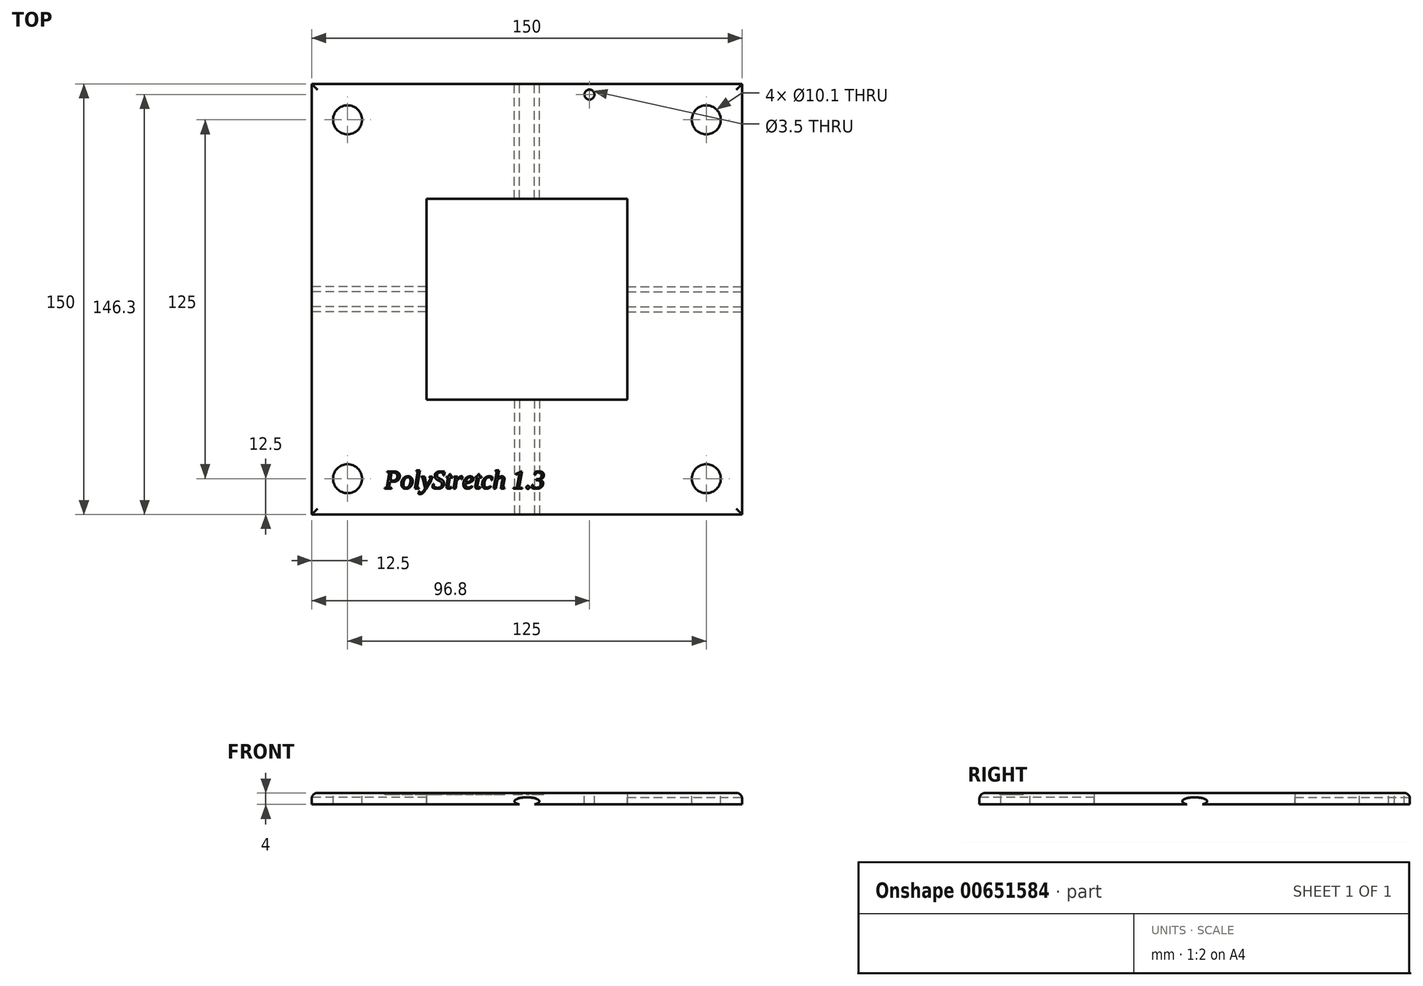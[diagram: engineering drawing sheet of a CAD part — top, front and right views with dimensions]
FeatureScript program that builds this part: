
annotation { "Feature Type Name" : "Feature", "Feature Type Description" : "" }
export const myFeature = defineFeature(function(context is Context, id is Id, definition is map)
    precondition{}
    {
        {
            var Q0;
            Q0=qCreatedBy(makeId("Top.planeOp"),FACE);
            var sketch = newSketch(context, id + "F0", { "sketchPlane" : qUnion([Q0])});
            skLineSegment(sketch, "E0.bottom", {"start": v(75, 75) * mm, "end": v(-75, 75) * mm});
            skLineSegment(sketch, "E0.top", {"start": v(75, -75) * mm, "end": v(-75, -75) * mm});
            skLineSegment(sketch, "E0.left", {"start": v(75, 75) * mm, "end": v(75, -75) * mm});
            skLineSegment(sketch, "E0.right", {"start": v(-75, 75) * mm, "end": v(-75, -75) * mm});
            skPoint(sketch, "E0.middle", {"position": v(0, 0) * mm});
            skLineSegment(sketch, "E1.bottom", {"start": v(35, 35) * mm, "end": v(-35, 35) * mm});
            skLineSegment(sketch, "E1.top", {"start": v(35, -35) * mm, "end": v(-35, -35) * mm});
            skLineSegment(sketch, "E1.left", {"start": v(35, 35) * mm, "end": v(35, -35) * mm});
            skLineSegment(sketch, "E1.right", {"start": v(-35, 35) * mm, "end": v(-35, -35) * mm});
            skSolve(sketch);
        }
        {
            var Q0;
            Q0=makeQuery(id+"F0.imprint","IMPRINT",FACE,{"disambiguationData":[TD([[makeQuery(id+"F0.imprint","IMPRINT",EDGE,{"derivedFrom":sQuery(id+"F0.wireOp",EDGE,"E0.bottom")}),1.0]])]});
            var Q1;
            Q1=makeQuery(id+"F0.imprint","IMPRINT",FACE,{"disambiguationData":[TD([[makeQuery(id+"F0.imprint","IMPRINT",EDGE,{"derivedFrom":sQuery(id+"F0.wireOp",EDGE,"3oa3hqku-FSQT-L0BX-7M5J-21aA9cYNgIiB")}),1.0]])]});
            extrude(context, id + "F1", {"entities" : qUnion([Q0, Q1]), "depth" : 4 * mm});
        }
        {
            var Q0;
            Q0=makeQuery(id+"F1.opExtrude","CAP_FACE",FACE,{"disambiguationData":[OSD([sQuery(id+"F0.wireOp",EDGE,"E0.bottom"),sQuery(id+"F0.wireOp",EDGE,"E0.top"),sQuery(id+"F0.wireOp",EDGE,"E0.left"),sQuery(id+"F0.wireOp",EDGE,"E0.right"),sQuery(id+"F0.wireOp",EDGE,"E1.bottom"),sQuery(id+"F0.wireOp",EDGE,"E1.top"),sQuery(id+"F0.wireOp",EDGE,"E1.left"),sQuery(id+"F0.wireOp",EDGE,"E1.right")])],"isStart":false});
            var sketch = newSketch(context, id + "F2", { "sketchPlane" : qUnion([Q0])});
            skLineSegment(sketch, "E2", {"start": v(-62.5, -75) * mm, "end": v(-62.5, -62.5) * mm, "construction": true});
            skLineSegment(sketch, "E3", {"start": v(-62.5, -62.5) * mm, "end": v(-75, -62.5) * mm, "construction": true});
            skCircle(sketch, "E4", {"center": v(-62.5, -62.5) * mm, "radius": 5.05 * mm});
            skLineSegment(sketch, "E5", {"start": v(-62.5, 75) * mm, "end": v(-62.5, 62.5) * mm, "construction": true});
            skLineSegment(sketch, "E6", {"start": v(-62.5, 62.5) * mm, "end": v(-75, 62.5) * mm, "construction": true});
            skLineSegment(sketch, "E7", {"start": v(62.5, 75) * mm, "end": v(62.5, 62.5) * mm, "construction": true});
            skLineSegment(sketch, "E8", {"start": v(62.5, 62.5) * mm, "end": v(75, 62.5) * mm, "construction": true});
            skLineSegment(sketch, "E9", {"start": v(75, -62.5) * mm, "end": v(62.5, -62.5) * mm, "construction": true});
            skLineSegment(sketch, "E10", {"start": v(62.5, -62.5) * mm, "end": v(62.5, -75) * mm, "construction": true});
            skCircle(sketch, "E11", {"center": v(-62.5, 62.5) * mm, "radius": 5.05 * mm});
            skCircle(sketch, "E12", {"center": v(62.5, 62.5) * mm, "radius": 5.05 * mm});
            skCircle(sketch, "E13", {"center": v(62.5, -62.5) * mm, "radius": 5.05 * mm});
            skSolve(sketch);
        }
        {
            var Q0;
            Q0=makeQuery(id+"F2.imprint","IMPRINT",FACE,{"disambiguationData":[TD([[makeQuery(id+"F2.imprint","IMPRINT",EDGE,{"derivedFrom":sQuery(id+"F2.wireOp",EDGE,"E12")}),1.0]])]});
            var Q1;
            Q1=makeQuery(id+"F2.imprint","IMPRINT",FACE,{"disambiguationData":[TD([[makeQuery(id+"F2.imprint","IMPRINT",EDGE,{"derivedFrom":sQuery(id+"F2.wireOp",EDGE,"E11")}),1.0]])]});
            var Q2;
            Q2=makeQuery(id+"F2.imprint","IMPRINT",FACE,{"disambiguationData":[TD([[makeQuery(id+"F2.imprint","IMPRINT",EDGE,{"derivedFrom":sQuery(id+"F2.wireOp",EDGE,"E4")}),1.0]])]});
            var Q3;
            Q3=makeQuery(id+"F2.imprint","IMPRINT",FACE,{"disambiguationData":[TD([[makeQuery(id+"F2.imprint","IMPRINT",EDGE,{"derivedFrom":sQuery(id+"F2.wireOp",EDGE,"E13")}),1.0]])]});
            extrude(context, id + "F3", {"entities" : qUnion([Q0, Q1, Q2, Q3]), "operationType" : NewBodyOperationType.REMOVE, "oppositeDirection" : true, "depth" : 4 * mm});
        }
        {
            var Q0;
            Q0=makeQuery(id+"F1.opExtrude","CAP_FACE",FACE,{"disambiguationData":[OSD([sQuery(id+"F0.wireOp",EDGE,"E0.bottom"),sQuery(id+"F0.wireOp",EDGE,"E0.top"),sQuery(id+"F0.wireOp",EDGE,"E0.left"),sQuery(id+"F0.wireOp",EDGE,"E0.right"),sQuery(id+"F0.wireOp",EDGE,"E1.bottom"),sQuery(id+"F0.wireOp",EDGE,"E1.top"),sQuery(id+"F0.wireOp",EDGE,"E1.left"),sQuery(id+"F0.wireOp",EDGE,"E1.right")])],"isStart":false});
            var sketch = newSketch(context, id + "F4", { "sketchPlane" : qUnion([Q0])});
            skText(sketch, "E14", { "text": "PolyStretch 1.3", "fontName": "Tinos-Italic.ttf"});
            const initialGuessF4  = {"E14": [-0.0496, -0.06594, 1, 0, 0.00652]};
            skSetInitialGuess(sketch, initialGuessF4);
            skSolve(sketch);
        }
        {
            var Q0;
            Q0=qSketchRegion(id+"F4",true);
            extrude(context, id + "F5", {"entities" : qUnion([Q0]), "operationType" : NewBodyOperationType.REMOVE, "oppositeDirection" : true, "depth" : 0.5 * mm});
        }
        {
            var Q0;
            Q0=makeQuery(id+"F1.opExtrude","SWEPT_FACE",FACE,{"disambiguationData":[OSD([sQuery(id+"F0.wireOp",EDGE,"E0.top")])]});
            var sketch = newSketch(context, id + "F6", { "sketchPlane" : qUnion([Q0])});
            skPoint(sketch, "E15.centerSnap0", {"position": v(0, 0) * mm});
            skLineSegment(sketch, "E16", {"start": v(0, 0) * mm, "end": v(0, 1.1) * mm, "construction": true});
            skEllipse(sketch, "E17", {"center": v(0, 1.1) * mm, "majorRadius": 4.33 * mm, "minorRadius": 1.38 * mm, "majorAxis": v(-1, 0)});
            skSolve(sketch);
        }
        {
            var Q0;
            {var subQ0=sQuery(id+"F6.wireOp",EDGE,"E17");var subQ1=makeQuery(id+"F1.opExtrude","CAP_EDGE",EDGE,{"disambiguationData":[OSD([sQuery(id+"F0.wireOp",EDGE,"E0.top")])],"isStart":true});var subQ2=makeQuery(id+"F6.imprint","INTERSECT",VERTEX,{"disambiguationData":[OD(0.0)],"derivedFrom":[subQ1,subQ0]});Q0=makeQuery(id+"F6.imprint","IMPRINT",FACE,{"disambiguationData":[TD([[makeQuery(id+"F6.imprint","IMPRINT",EDGE,{"disambiguationData":[TD([[subQ2,-1.0]])],"derivedFrom":subQ0}),1.0]])]});}
            extrude(context, id + "F7", {"entities" : qUnion([Q0]), "operationType" : NewBodyOperationType.REMOVE, "oppositeDirection" : true, "depth" : 50 * mm});
        }
        {
            var Q0;
            Q0=makeQuery(id+"F1.opExtrude","SWEPT_FACE",FACE,{"disambiguationData":[OSD([sQuery(id+"F0.wireOp",EDGE,"E0.left")])]});
            var sketch = newSketch(context, id + "F8", { "sketchPlane" : qUnion([Q0])});
            skPoint(sketch, "E18.centerSnap0", {"position": v(0, 0) * mm});
            skLineSegment(sketch, "E19", {"start": v(0, 0) * mm, "end": v(0, 1.1) * mm, "construction": true});
            skEllipse(sketch, "E20", {"center": v(0, 1.1) * mm, "majorRadius": 4.33 * mm, "minorRadius": 1.38 * mm, "majorAxis": v(1, 0)});
            skSolve(sketch);
        }
        {
            var Q0;
            Q0=qSketchRegion(id+"F8",true);
            extrude(context, id + "F9", {"entities" : qUnion([Q0]), "operationType" : NewBodyOperationType.REMOVE, "oppositeDirection" : true, "depth" : 50 * mm});
        }
        {
            var Q0;
            Q0=makeQuery(id+"F1.opExtrude","SWEPT_FACE",FACE,{"disambiguationData":[OSD([sQuery(id+"F0.wireOp",EDGE,"E0.right")])]});
            var sketch = newSketch(context, id + "F10", { "sketchPlane" : qUnion([Q0])});
            skLineSegment(sketch, "E21", {"start": v(0, 0) * mm, "end": v(0, 1.1) * mm, "construction": true});
            skEllipse(sketch, "E22", {"center": v(0, 1.1) * mm, "majorRadius": 4.33 * mm, "minorRadius": 1.38 * mm, "majorAxis": v(-1, 0)});
            skSolve(sketch);
        }
        {
            var Q0;
            {var subQ0=sQuery(id+"F10.wireOp",EDGE,"E22");var subQ1=makeQuery(id+"F1.opExtrude","CAP_EDGE",EDGE,{"disambiguationData":[OSD([sQuery(id+"F0.wireOp",EDGE,"E0.right")])],"isStart":true});var subQ2=makeQuery(id+"F10.imprint","INTERSECT",VERTEX,{"disambiguationData":[OD(0.0)],"derivedFrom":[subQ1,subQ0]});Q0=makeQuery(id+"F10.imprint","IMPRINT",FACE,{"disambiguationData":[TD([[makeQuery(id+"F10.imprint","IMPRINT",EDGE,{"disambiguationData":[TD([[subQ2,1.0]])],"derivedFrom":subQ0}),1.0]])]});}
            extrude(context, id + "F11", {"entities" : qUnion([Q0]), "operationType" : NewBodyOperationType.REMOVE, "oppositeDirection" : true, "depth" : 50 * mm});
        }
        {
            var Q0;
            Q0=makeQuery(id+"F1.opExtrude","SWEPT_FACE",FACE,{"disambiguationData":[OSD([sQuery(id+"F0.wireOp",EDGE,"E0.bottom")])]});
            var sketch = newSketch(context, id + "F12", { "sketchPlane" : qUnion([Q0])});
            skLineSegment(sketch, "E23", {"start": v(0, 0) * mm, "end": v(0, 1.1) * mm, "construction": true});
            skEllipse(sketch, "E24", {"center": v(0, 1.1) * mm, "majorRadius": 4.33 * mm, "minorRadius": 1.38 * mm, "majorAxis": v(-1, 0)});
            skSolve(sketch);
        }
        {
            var Q0;
            {var subQ0=sQuery(id+"F12.wireOp",EDGE,"E24");var subQ1=makeQuery(id+"F1.opExtrude","CAP_EDGE",EDGE,{"disambiguationData":[OSD([sQuery(id+"F0.wireOp",EDGE,"E0.bottom")])],"isStart":true});var subQ2=makeQuery(id+"F12.imprint","INTERSECT",VERTEX,{"disambiguationData":[OD(0.0)],"derivedFrom":[subQ1,subQ0]});Q0=makeQuery(id+"F12.imprint","IMPRINT",FACE,{"disambiguationData":[TD([[makeQuery(id+"F12.imprint","IMPRINT",EDGE,{"disambiguationData":[TD([[subQ2,1.0]])],"derivedFrom":subQ0}),1.0]])]});}
            extrude(context, id + "F13", {"entities" : qUnion([Q0]), "operationType" : NewBodyOperationType.REMOVE, "oppositeDirection" : true, "depth" : 50 * mm});
        }
        {
            var Q0;
            Q0=makeQuery(id+"F1.opExtrude","CAP_EDGE",EDGE,{"disambiguationData":[OSD([sQuery(id+"F0.wireOp",EDGE,"E0.left")])],"isStart":false});
            var Q1;
            Q1=makeQuery(id+"F1.opExtrude","CAP_EDGE",EDGE,{"disambiguationData":[OSD([sQuery(id+"F0.wireOp",EDGE,"E0.bottom")])],"isStart":false});
            var Q2;
            Q2=makeQuery(id+"F1.opExtrude","CAP_EDGE",EDGE,{"disambiguationData":[OSD([sQuery(id+"F0.wireOp",EDGE,"E0.top")])],"isStart":false});
            var Q3;
            Q3=makeQuery(id+"F1.opExtrude","CAP_EDGE",EDGE,{"disambiguationData":[OSD([sQuery(id+"F0.wireOp",EDGE,"E0.right")])],"isStart":false});
            fillet(context, id + "F14", {"entities" : qUnion([Q0, Q1, Q2, Q3]), "radius" : 2 * mm, "tangentPropagation" : true, "allowEdgeOverflow" : false});
        }
        {
            var Q0;
            {var subQ0=sQuery(id+"F0.wireOp",EDGE,"E1.left");var subQ1=sQuery(id+"F0.wireOp",EDGE,"E1.right");var subQ2=sQuery(id+"F0.wireOp",EDGE,"E1.top");var subQ3=sQuery(id+"F0.wireOp",EDGE,"E0.bottom");var subQ4=sQuery(id+"F0.wireOp",EDGE,"E0.top");var subQ5=sQuery(id+"F0.wireOp",EDGE,"E1.bottom");var subQ6=sQuery(id+"F0.wireOp",EDGE,"E0.left");var subQ7=sQuery(id+"F0.wireOp",EDGE,"E0.right");Q0=makeQuery(id+"F5.boolean.opBoolean","SPLIT",FACE,{"disambiguationData":[TD([makeQuery(id+"F1.opExtrude","SWEPT_FACE",FACE,{"disambiguationData":[OSD([subQ3])]})])],"derivedFrom":makeQuery(id+"F1.opExtrude","CAP_FACE",FACE,{"disambiguationData":[OSD([subQ3,subQ4,subQ6,subQ7,subQ5,subQ2,subQ0,subQ1])],"isStart":false})});}
            var sketch = newSketch(context, id + "F15", { "sketchPlane" : qUnion([Q0])});
            skLineSegment(sketch, "E25", {"start": v(73, 71.3) * mm, "end": v(21.8, 71.3) * mm, "construction": true});
            skLineSegment(sketch, "E26", {"start": v(21.8, 71.3) * mm, "end": v(21.8, 73) * mm, "construction": true});
            skCircle(sketch, "E27", {"center": v(21.8, 71.3) * mm, "radius": 1.75 * mm});
            skLineSegment(sketch, "E28", {"start": v(21.8, 71.3) * mm, "end": v(21.8, 59.6) * mm, "construction": true});
            skLineSegment(sketch, "E29", {"start": v(21.8, 59.6) * mm, "end": v(63.9, 59.6) * mm, "construction": true});
            skCircle(sketch, "E30", {"center": v(63.9, 59.6) * mm, "radius": 1.75 * mm});
            skLineSegment(sketch, "E31", {"start": v(62.5, 62.5) * mm, "end": v(63.9, 59.6) * mm, "construction": true});
            skLineSegment(sketch, "E32", {"start": v(62.5, 62.5) * mm, "end": v(62.5, 57.45) * mm, "construction": true});
            skSolve(sketch);
        }
        {
            var Q0;
            {var subQ0=sQuery(id+"F15.wireOp",EDGE,"E27");var subQ1=sQuery(id+"F0.wireOp",EDGE,"E1.left");var subQ2=sQuery(id+"F0.wireOp",EDGE,"E1.right");var subQ3=sQuery(id+"F0.wireOp",EDGE,"E1.top");var subQ4=sQuery(id+"F0.wireOp",EDGE,"E0.bottom");var subQ5=sQuery(id+"F0.wireOp",EDGE,"E0.top");var subQ6=sQuery(id+"F0.wireOp",EDGE,"E1.bottom");var subQ7=sQuery(id+"F0.wireOp",EDGE,"E0.left");var subQ8=sQuery(id+"F0.wireOp",EDGE,"E0.right");var subQ9=makeQuery(id+"F14.opFillet","BLEND_EDGE",EDGE,{"blendedFrom":[makeQuery(id+"F1.opExtrude","CAP_EDGE",EDGE,{"disambiguationData":[OSD([subQ4])],"isStart":false}),makeQuery(id+"F5.boolean.opBoolean","SPLIT",FACE,{"disambiguationData":[TD([makeQuery(id+"F1.opExtrude","SWEPT_FACE",FACE,{"disambiguationData":[OSD([subQ4])]})])],"derivedFrom":makeQuery(id+"F1.opExtrude","CAP_FACE",FACE,{"disambiguationData":[OSD([subQ4,subQ5,subQ7,subQ8,subQ6,subQ3,subQ1,subQ2])],"isStart":false})})],"blendedInto":[makeQuery(id+"F5.boolean.opBoolean","SPLIT",FACE,{"disambiguationData":[TD([makeQuery(id+"F1.opExtrude","SWEPT_FACE",FACE,{"disambiguationData":[OSD([subQ4])]})])],"derivedFrom":makeQuery(id+"F1.opExtrude","CAP_FACE",FACE,{"disambiguationData":[OSD([subQ4,subQ5,subQ7,subQ8,subQ6,subQ3,subQ1,subQ2])],"isStart":false})})]});var subQ10=makeQuery(id+"F15.imprint","INTERSECT",VERTEX,{"disambiguationData":[OD(0.0)],"derivedFrom":[subQ9,subQ0]});Q0=makeQuery(id+"F15.imprint","IMPRINT",FACE,{"disambiguationData":[TD([[makeQuery(id+"F15.imprint","IMPRINT",EDGE,{"disambiguationData":[TD([[subQ10,1.0]])],"derivedFrom":subQ0}),1.0]])]});}
            var Q1;
            {var subQ0=sQuery(id+"F15.wireOp",EDGE,"E27");var subQ1=sQuery(id+"F0.wireOp",EDGE,"E1.left");var subQ2=sQuery(id+"F0.wireOp",EDGE,"E1.right");var subQ3=sQuery(id+"F0.wireOp",EDGE,"E1.top");var subQ4=sQuery(id+"F0.wireOp",EDGE,"E0.bottom");var subQ5=sQuery(id+"F0.wireOp",EDGE,"E0.top");var subQ6=sQuery(id+"F0.wireOp",EDGE,"E1.bottom");var subQ7=sQuery(id+"F0.wireOp",EDGE,"E0.left");var subQ8=sQuery(id+"F0.wireOp",EDGE,"E0.right");var subQ9=makeQuery(id+"F14.opFillet","BLEND_EDGE",EDGE,{"blendedFrom":[makeQuery(id+"F1.opExtrude","CAP_EDGE",EDGE,{"disambiguationData":[OSD([subQ4])],"isStart":false}),makeQuery(id+"F5.boolean.opBoolean","SPLIT",FACE,{"disambiguationData":[TD([makeQuery(id+"F1.opExtrude","SWEPT_FACE",FACE,{"disambiguationData":[OSD([subQ4])]})])],"derivedFrom":makeQuery(id+"F1.opExtrude","CAP_FACE",FACE,{"disambiguationData":[OSD([subQ4,subQ5,subQ7,subQ8,subQ6,subQ3,subQ1,subQ2])],"isStart":false})})],"blendedInto":[makeQuery(id+"F5.boolean.opBoolean","SPLIT",FACE,{"disambiguationData":[TD([makeQuery(id+"F1.opExtrude","SWEPT_FACE",FACE,{"disambiguationData":[OSD([subQ4])]})])],"derivedFrom":makeQuery(id+"F1.opExtrude","CAP_FACE",FACE,{"disambiguationData":[OSD([subQ4,subQ5,subQ7,subQ8,subQ6,subQ3,subQ1,subQ2])],"isStart":false})})]});var subQ10=makeQuery(id+"F15.imprint","INTERSECT",VERTEX,{"disambiguationData":[OD(0.0)],"derivedFrom":[subQ9,subQ0]});Q1=makeQuery(id+"F15.imprint","IMPRINT",FACE,{"disambiguationData":[TD([[makeQuery(id+"F15.imprint","IMPRINT",EDGE,{"disambiguationData":[TD([[subQ10,-1.0]])],"derivedFrom":subQ0}),1.0]])]});}
            extrude(context, id + "F16", {"entities" : qUnion([Q0, Q1]), "operationType" : NewBodyOperationType.REMOVE, "oppositeDirection" : true, "depth" : 25 * mm});
        }
    });
